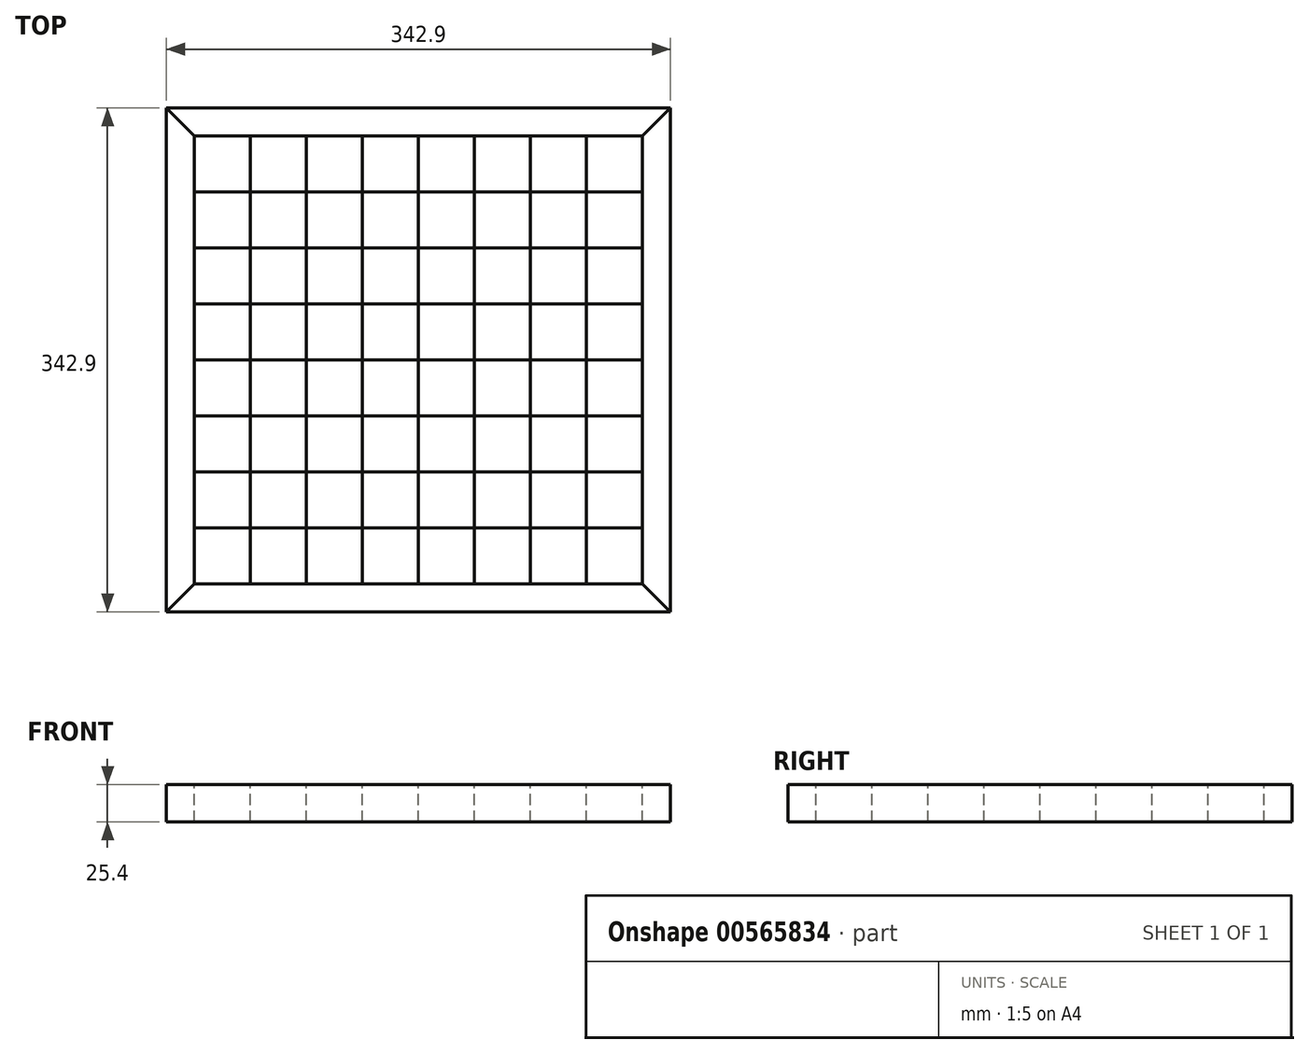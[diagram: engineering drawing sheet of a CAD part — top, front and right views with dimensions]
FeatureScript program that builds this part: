
annotation { "Feature Type Name" : "Feature", "Feature Type Description" : "" }
export const myFeature = defineFeature(function(context is Context, id is Id, definition is map)
    precondition{}
    {
        {
            var Q0;
            Q0=qCreatedBy(makeId("Top.planeOp"),FACE);
            var sketch = newSketch(context, id + "F0", { "sketchPlane" : qUnion([Q0])});
            skLineSegment(sketch, "E0.bottom", {"start": v(-171.45, 171.45) * mm, "end": v(171.45, 171.45) * mm});
            skLineSegment(sketch, "E0.top", {"start": v(-171.45, -171.45) * mm, "end": v(171.45, -171.45) * mm});
            skLineSegment(sketch, "E0.left", {"start": v(-171.45, 171.45) * mm, "end": v(-171.45, -171.45) * mm});
            skLineSegment(sketch, "E0.right", {"start": v(171.45, 171.45) * mm, "end": v(171.45, -171.45) * mm});
            skPoint(sketch, "E0.middle", {"position": v(0, 0) * mm});
            skSolve(sketch);
        }
        {
            var Q0;
            Q0=makeQuery(id+"F0.imprint","IMPRINT",FACE,{"disambiguationData":[TD([[makeQuery(id+"F0.imprint","IMPRINT",EDGE,{"derivedFrom":sQuery(id+"F0.wireOp",EDGE,"E0.bottom")}),-1.0]])]});
            var sketch = newSketch(context, id + "F1", { "sketchPlane" : qUnion([Q0])});
            skLineSegment(sketch, "E1.bottom", {"start": v(-152.4, 152.4) * mm, "end": v(152.4, 152.4) * mm});
            skLineSegment(sketch, "E1.top", {"start": v(-152.4, -152.4) * mm, "end": v(152.4, -152.4) * mm});
            skLineSegment(sketch, "E1.left", {"start": v(-152.4, 152.4) * mm, "end": v(-152.4, -152.4) * mm});
            skLineSegment(sketch, "E1.right", {"start": v(152.4, 152.4) * mm, "end": v(152.4, -152.4) * mm});
            skPoint(sketch, "E1.middle", {"position": v(0, 0) * mm});
            skLineSegment(sketch, "E2", {"start": v(-114.3, -152.4) * mm, "end": v(-114.3, 152.4) * mm});
            skLineSegment(sketch, "E3", {"start": v(-152.4, -114.3) * mm, "end": v(152.4, -114.3) * mm});
            skLineSegment(sketch, "E4", {"start": v(-152.4, -76.2) * mm, "end": v(152.4, -76.2) * mm});
            skLineSegment(sketch, "E5", {"start": v(-152.4, -38.1) * mm, "end": v(152.4, -38.1) * mm});
            skLineSegment(sketch, "E6", {"start": v(-152.4, 0) * mm, "end": v(152.4, 0) * mm});
            skLineSegment(sketch, "E7", {"start": v(-152.4, 38.1) * mm, "end": v(152.4, 38.1) * mm});
            skLineSegment(sketch, "E8", {"start": v(-152.4, 76.2) * mm, "end": v(152.4, 76.2) * mm});
            skLineSegment(sketch, "E9", {"start": v(-152.4, 114.3) * mm, "end": v(152.4, 114.3) * mm});
            skLineSegment(sketch, "E10", {"start": v(-76.2, -152.4) * mm, "end": v(-76.2, 152.4) * mm});
            skLineSegment(sketch, "E11", {"start": v(-38.1, -152.4) * mm, "end": v(-38.1, 152.4) * mm});
            skLineSegment(sketch, "E12", {"start": v(0, -152.4) * mm, "end": v(0, 152.4) * mm});
            skLineSegment(sketch, "E13", {"start": v(38.1, -152.4) * mm, "end": v(38.1, 152.4) * mm});
            skLineSegment(sketch, "E14", {"start": v(76.2, -152.4) * mm, "end": v(76.2, 152.4) * mm});
            skLineSegment(sketch, "E15", {"start": v(114.3, -152.4) * mm, "end": v(114.3, 152.4) * mm});
            skSolve(sketch);
        }
        {
            var Q0;
            Q0=makeQuery(id+"F0.imprint","IMPRINT",FACE,{"disambiguationData":[TD([[makeQuery(id+"F0.imprint","IMPRINT",EDGE,{"derivedFrom":sQuery(id+"F0.wireOp",EDGE,"E0.bottom")}),-1.0]])]});
            var sketch = newSketch(context, id + "F2", { "sketchPlane" : qUnion([Q0])});
            skPoint(sketch, "E16.0", {"position": v(-171.45, -171.45) * mm});
            skPoint(sketch, "E17.0", {"position": v(-152.4, -152.4) * mm});
            skPoint(sketch, "E18.0", {"position": v(152.4, -152.4) * mm});
            skPoint(sketch, "E19.0", {"position": v(171.45, -171.45) * mm});
            skPoint(sketch, "E20.0", {"position": v(152.4, 152.4) * mm});
            skPoint(sketch, "E21.0", {"position": v(171.45, 171.45) * mm});
            skPoint(sketch, "E22.0", {"position": v(-152.4, 152.4) * mm});
            skPoint(sketch, "E23.0", {"position": v(-171.45, 171.45) * mm});
            skLineSegment(sketch, "E24.0", {"start": v(-152.4, 152.4) * mm, "end": v(-152.4, -152.4) * mm});
            skLineSegment(sketch, "E25.0", {"start": v(-171.45, 171.45) * mm, "end": v(-171.45, -171.45) * mm});
            skLineSegment(sketch, "E26", {"start": v(-152.4, 152.4) * mm, "end": v(-171.45, 171.45) * mm});
            skLineSegment(sketch, "E27", {"start": v(-171.45, -171.45) * mm, "end": v(-152.4, -152.4) * mm});
            skLineSegment(sketch, "E28.0", {"start": v(-152.4, -152.4) * mm, "end": v(152.4, -152.4) * mm});
            skLineSegment(sketch, "E29.0", {"start": v(-171.45, -171.45) * mm, "end": v(171.45, -171.45) * mm});
            skLineSegment(sketch, "E30", {"start": v(171.45, -171.45) * mm, "end": v(152.4, -152.4) * mm});
            skLineSegment(sketch, "E31.0", {"start": v(171.45, 171.45) * mm, "end": v(171.45, -171.45) * mm});
            skLineSegment(sketch, "E32.0", {"start": v(152.4, 152.4) * mm, "end": v(152.4, -152.4) * mm});
            skLineSegment(sketch, "E33.0", {"start": v(-152.4, 152.4) * mm, "end": v(152.4, 152.4) * mm});
            skLineSegment(sketch, "E34.0", {"start": v(-171.45, 171.45) * mm, "end": v(171.45, 171.45) * mm});
            skLineSegment(sketch, "E35", {"start": v(152.4, 152.4) * mm, "end": v(171.45, 171.45) * mm});
            skSolve(sketch);
        }
        {
            var Q0;
            {var subQ0=sQuery(id+"F1.wireOp",EDGE,"E1.left");var subQ1=sQuery(id+"F1.wireOp",EDGE,"E1.top");var subQ2=makeQuery(id+"F1.imprint","INTERSECT",VERTEX,{"derivedFrom":[subQ1,subQ0]});Q0=makeQuery(id+"F1.imprint","IMPRINT",FACE,{"disambiguationData":[TD([[makeQuery(id+"F1.imprint","IMPRINT",EDGE,{"disambiguationData":[TD([[subQ2,-1.0]])],"derivedFrom":subQ1}),1.0]])]});}
            extrude(context, id + "F3", {"entities" : qUnion([Q0]), "oppositeDirection" : true, "depth" : 25.4 * mm, "offsetDistance" : 25.4 * mm});
        }
        {
            var Q0;
            {var subQ0=sQuery(id+"F1.wireOp",EDGE,"E3");var subQ1=sQuery(id+"F1.wireOp",EDGE,"E1.left");var subQ2=makeQuery(id+"F1.imprint","INTERSECT",VERTEX,{"derivedFrom":[subQ1,subQ0]});Q0=makeQuery(id+"F1.imprint","IMPRINT",FACE,{"disambiguationData":[TD([[makeQuery(id+"F1.imprint","IMPRINT",EDGE,{"disambiguationData":[TD([[subQ2,1.0]])],"derivedFrom":subQ1}),1.0]])]});}
            extrude(context, id + "F4", {"entities" : qUnion([Q0]), "oppositeDirection" : true, "depth" : 25.4 * mm, "offsetDistance" : 25.4 * mm});
        }
        {
            var Q0;
            {var subQ0=sQuery(id+"F1.wireOp",EDGE,"E6");var subQ1=sQuery(id+"F1.wireOp",EDGE,"E1.left");var subQ2=makeQuery(id+"F1.imprint","INTERSECT",VERTEX,{"derivedFrom":[subQ1,subQ0]});Q0=makeQuery(id+"F1.imprint","IMPRINT",FACE,{"disambiguationData":[TD([[makeQuery(id+"F1.imprint","IMPRINT",EDGE,{"disambiguationData":[TD([[subQ2,1.0]])],"derivedFrom":subQ1}),1.0]])]});}
            extrude(context, id + "F5", {"entities" : qUnion([Q0]), "oppositeDirection" : true, "depth" : 25.4 * mm, "offsetDistance" : 25.4 * mm});
        }
        {
            var Q0;
            {var subQ0=sQuery(id+"F1.wireOp",EDGE,"E4");var subQ1=sQuery(id+"F1.wireOp",EDGE,"E1.left");var subQ2=makeQuery(id+"F1.imprint","INTERSECT",VERTEX,{"derivedFrom":[subQ1,subQ0]});Q0=makeQuery(id+"F1.imprint","IMPRINT",FACE,{"disambiguationData":[TD([[makeQuery(id+"F1.imprint","IMPRINT",EDGE,{"disambiguationData":[TD([[subQ2,1.0]])],"derivedFrom":subQ1}),1.0]])]});}
            extrude(context, id + "F6", {"entities" : qUnion([Q0]), "oppositeDirection" : true, "depth" : 25.4 * mm, "offsetDistance" : 25.4 * mm});
        }
        {
            var Q0;
            {var subQ0=sQuery(id+"F1.wireOp",EDGE,"E5");var subQ1=sQuery(id+"F1.wireOp",EDGE,"E1.left");var subQ2=makeQuery(id+"F1.imprint","INTERSECT",VERTEX,{"derivedFrom":[subQ1,subQ0]});Q0=makeQuery(id+"F1.imprint","IMPRINT",FACE,{"disambiguationData":[TD([[makeQuery(id+"F1.imprint","IMPRINT",EDGE,{"disambiguationData":[TD([[subQ2,1.0]])],"derivedFrom":subQ1}),1.0]])]});}
            extrude(context, id + "F7", {"entities" : qUnion([Q0]), "oppositeDirection" : true, "depth" : 25.4 * mm, "offsetDistance" : 25.4 * mm});
        }
        {
            var Q0;
            {var subQ0=sQuery(id+"F1.wireOp",EDGE,"E7");var subQ1=sQuery(id+"F1.wireOp",EDGE,"E1.left");var subQ2=makeQuery(id+"F1.imprint","INTERSECT",VERTEX,{"derivedFrom":[subQ1,subQ0]});Q0=makeQuery(id+"F1.imprint","IMPRINT",FACE,{"disambiguationData":[TD([[makeQuery(id+"F1.imprint","IMPRINT",EDGE,{"disambiguationData":[TD([[subQ2,1.0]])],"derivedFrom":subQ1}),1.0]])]});}
            extrude(context, id + "F8", {"entities" : qUnion([Q0]), "oppositeDirection" : true, "depth" : 25.4 * mm, "offsetDistance" : 25.4 * mm});
        }
        {
            var Q0;
            {var subQ0=sQuery(id+"F1.wireOp",EDGE,"E8");var subQ1=sQuery(id+"F1.wireOp",EDGE,"E1.left");var subQ2=makeQuery(id+"F1.imprint","INTERSECT",VERTEX,{"derivedFrom":[subQ1,subQ0]});Q0=makeQuery(id+"F1.imprint","IMPRINT",FACE,{"disambiguationData":[TD([[makeQuery(id+"F1.imprint","IMPRINT",EDGE,{"disambiguationData":[TD([[subQ2,1.0]])],"derivedFrom":subQ1}),1.0]])]});}
            extrude(context, id + "F9", {"entities" : qUnion([Q0]), "oppositeDirection" : true, "depth" : 25.4 * mm, "offsetDistance" : 25.4 * mm});
        }
        {
            var Q0;
            {var subQ0=sQuery(id+"F1.wireOp",EDGE,"E1.left");var subQ1=sQuery(id+"F1.wireOp",EDGE,"E1.bottom");var subQ2=makeQuery(id+"F1.imprint","INTERSECT",VERTEX,{"derivedFrom":[subQ1,subQ0]});Q0=makeQuery(id+"F1.imprint","IMPRINT",FACE,{"disambiguationData":[TD([[makeQuery(id+"F1.imprint","IMPRINT",EDGE,{"disambiguationData":[TD([[subQ2,-1.0]])],"derivedFrom":subQ1}),-1.0]])]});}
            extrude(context, id + "F10", {"entities" : qUnion([Q0]), "oppositeDirection" : true, "depth" : 25.4 * mm, "offsetDistance" : 25.4 * mm});
        }
        {
            var Q0;
            {var subQ0=sQuery(id+"F1.wireOp",EDGE,"E2");var subQ1=sQuery(id+"F1.wireOp",EDGE,"E1.bottom");var subQ2=makeQuery(id+"F1.imprint","INTERSECT",VERTEX,{"derivedFrom":[subQ1,subQ0]});Q0=makeQuery(id+"F1.imprint","IMPRINT",FACE,{"disambiguationData":[TD([[makeQuery(id+"F1.imprint","IMPRINT",EDGE,{"disambiguationData":[TD([[subQ2,-1.0]])],"derivedFrom":subQ1}),-1.0]])]});}
            extrude(context, id + "F11", {"entities" : qUnion([Q0]), "oppositeDirection" : true, "depth" : 25.4 * mm, "offsetDistance" : 25.4 * mm});
        }
        {
            var Q0;
            {var subQ0=sQuery(id+"F1.wireOp",EDGE,"E8");var subQ1=sQuery(id+"F1.wireOp",EDGE,"E2");var subQ2=makeQuery(id+"F1.imprint","INTERSECT",VERTEX,{"derivedFrom":[subQ1,subQ0]});Q0=makeQuery(id+"F1.imprint","IMPRINT",FACE,{"disambiguationData":[TD([[makeQuery(id+"F1.imprint","IMPRINT",EDGE,{"disambiguationData":[TD([[subQ2,-1.0]])],"derivedFrom":subQ1}),-1.0]])]});}
            extrude(context, id + "F12", {"entities" : qUnion([Q0]), "oppositeDirection" : true, "depth" : 25.4 * mm, "offsetDistance" : 25.4 * mm});
        }
        {
            var Q0;
            {var subQ0=sQuery(id+"F1.wireOp",EDGE,"E7");var subQ1=sQuery(id+"F1.wireOp",EDGE,"E2");var subQ2=makeQuery(id+"F1.imprint","INTERSECT",VERTEX,{"derivedFrom":[subQ1,subQ0]});Q0=makeQuery(id+"F1.imprint","IMPRINT",FACE,{"disambiguationData":[TD([[makeQuery(id+"F1.imprint","IMPRINT",EDGE,{"disambiguationData":[TD([[subQ2,-1.0]])],"derivedFrom":subQ1}),-1.0]])]});}
            extrude(context, id + "F13", {"entities" : qUnion([Q0]), "oppositeDirection" : true, "depth" : 25.4 * mm, "offsetDistance" : 25.4 * mm});
        }
        {
            var Q0;
            {var subQ0=sQuery(id+"F1.wireOp",EDGE,"E6");var subQ1=sQuery(id+"F1.wireOp",EDGE,"E2");var subQ2=makeQuery(id+"F1.imprint","INTERSECT",VERTEX,{"derivedFrom":[subQ1,subQ0]});Q0=makeQuery(id+"F1.imprint","IMPRINT",FACE,{"disambiguationData":[TD([[makeQuery(id+"F1.imprint","IMPRINT",EDGE,{"disambiguationData":[TD([[subQ2,-1.0]])],"derivedFrom":subQ1}),-1.0]])]});}
            extrude(context, id + "F14", {"entities" : qUnion([Q0]), "oppositeDirection" : true, "depth" : 25.4 * mm, "offsetDistance" : 25.4 * mm});
        }
        {
            var Q0;
            {var subQ0=sQuery(id+"F1.wireOp",EDGE,"E5");var subQ1=sQuery(id+"F1.wireOp",EDGE,"E2");var subQ2=makeQuery(id+"F1.imprint","INTERSECT",VERTEX,{"derivedFrom":[subQ1,subQ0]});Q0=makeQuery(id+"F1.imprint","IMPRINT",FACE,{"disambiguationData":[TD([[makeQuery(id+"F1.imprint","IMPRINT",EDGE,{"disambiguationData":[TD([[subQ2,-1.0]])],"derivedFrom":subQ1}),-1.0]])]});}
            extrude(context, id + "F15", {"entities" : qUnion([Q0]), "oppositeDirection" : true, "depth" : 25.4 * mm, "offsetDistance" : 25.4 * mm});
        }
        {
            var Q0;
            {var subQ0=sQuery(id+"F1.wireOp",EDGE,"E4");var subQ1=sQuery(id+"F1.wireOp",EDGE,"E2");var subQ2=makeQuery(id+"F1.imprint","INTERSECT",VERTEX,{"derivedFrom":[subQ1,subQ0]});Q0=makeQuery(id+"F1.imprint","IMPRINT",FACE,{"disambiguationData":[TD([[makeQuery(id+"F1.imprint","IMPRINT",EDGE,{"disambiguationData":[TD([[subQ2,-1.0]])],"derivedFrom":subQ1}),-1.0]])]});}
            extrude(context, id + "F16", {"entities" : qUnion([Q0]), "oppositeDirection" : true, "depth" : 25.4 * mm, "offsetDistance" : 25.4 * mm});
        }
        {
            var Q0;
            {var subQ0=sQuery(id+"F1.wireOp",EDGE,"E3");var subQ1=sQuery(id+"F1.wireOp",EDGE,"E2");var subQ2=makeQuery(id+"F1.imprint","INTERSECT",VERTEX,{"derivedFrom":[subQ1,subQ0]});Q0=makeQuery(id+"F1.imprint","IMPRINT",FACE,{"disambiguationData":[TD([[makeQuery(id+"F1.imprint","IMPRINT",EDGE,{"disambiguationData":[TD([[subQ2,-1.0]])],"derivedFrom":subQ1}),-1.0]])]});}
            extrude(context, id + "F17", {"entities" : qUnion([Q0]), "oppositeDirection" : true, "depth" : 25.4 * mm, "offsetDistance" : 25.4 * mm});
        }
        {
            var Q0;
            {var subQ0=sQuery(id+"F1.wireOp",EDGE,"E2");var subQ1=sQuery(id+"F1.wireOp",EDGE,"E1.top");var subQ2=makeQuery(id+"F1.imprint","INTERSECT",VERTEX,{"derivedFrom":[subQ1,subQ0]});Q0=makeQuery(id+"F1.imprint","IMPRINT",FACE,{"disambiguationData":[TD([[makeQuery(id+"F1.imprint","IMPRINT",EDGE,{"disambiguationData":[TD([[subQ2,-1.0]])],"derivedFrom":subQ1}),1.0]])]});}
            extrude(context, id + "F18", {"entities" : qUnion([Q0]), "oppositeDirection" : true, "depth" : 25.4 * mm, "offsetDistance" : 25.4 * mm});
        }
        {
            var Q0;
            {var subQ0=sQuery(id+"F1.wireOp",EDGE,"E10");var subQ1=sQuery(id+"F1.wireOp",EDGE,"E1.bottom");var subQ2=makeQuery(id+"F1.imprint","INTERSECT",VERTEX,{"derivedFrom":[subQ1,subQ0]});Q0=makeQuery(id+"F1.imprint","IMPRINT",FACE,{"disambiguationData":[TD([[makeQuery(id+"F1.imprint","IMPRINT",EDGE,{"disambiguationData":[TD([[subQ2,-1.0]])],"derivedFrom":subQ1}),-1.0]])]});}
            extrude(context, id + "F19", {"entities" : qUnion([Q0]), "oppositeDirection" : true, "depth" : 25.4 * mm, "offsetDistance" : 25.4 * mm});
        }
        {
            var Q0;
            {var subQ0=sQuery(id+"F1.wireOp",EDGE,"E10");var subQ1=sQuery(id+"F1.wireOp",EDGE,"E8");var subQ2=makeQuery(id+"F1.imprint","INTERSECT",VERTEX,{"derivedFrom":[subQ1,subQ0]});Q0=makeQuery(id+"F1.imprint","IMPRINT",FACE,{"disambiguationData":[TD([[makeQuery(id+"F1.imprint","IMPRINT",EDGE,{"disambiguationData":[TD([[subQ2,-1.0]])],"derivedFrom":subQ1}),1.0]])]});}
            extrude(context, id + "F20", {"entities" : qUnion([Q0]), "oppositeDirection" : true, "depth" : 25.4 * mm, "offsetDistance" : 25.4 * mm});
        }
        {
            var Q0;
            {var subQ0=sQuery(id+"F1.wireOp",EDGE,"E10");var subQ1=sQuery(id+"F1.wireOp",EDGE,"E7");var subQ2=makeQuery(id+"F1.imprint","INTERSECT",VERTEX,{"derivedFrom":[subQ1,subQ0]});Q0=makeQuery(id+"F1.imprint","IMPRINT",FACE,{"disambiguationData":[TD([[makeQuery(id+"F1.imprint","IMPRINT",EDGE,{"disambiguationData":[TD([[subQ2,-1.0]])],"derivedFrom":subQ1}),1.0]])]});}
            extrude(context, id + "F21", {"entities" : qUnion([Q0]), "oppositeDirection" : true, "depth" : 25.4 * mm, "offsetDistance" : 25.4 * mm});
        }
        {
            var Q0;
            {var subQ0=sQuery(id+"F1.wireOp",EDGE,"E10");var subQ1=sQuery(id+"F1.wireOp",EDGE,"E6");var subQ2=makeQuery(id+"F1.imprint","INTERSECT",VERTEX,{"derivedFrom":[subQ1,subQ0]});Q0=makeQuery(id+"F1.imprint","IMPRINT",FACE,{"disambiguationData":[TD([[makeQuery(id+"F1.imprint","IMPRINT",EDGE,{"disambiguationData":[TD([[subQ2,-1.0]])],"derivedFrom":subQ1}),1.0]])]});}
            extrude(context, id + "F22", {"entities" : qUnion([Q0]), "oppositeDirection" : true, "depth" : 25.4 * mm, "offsetDistance" : 25.4 * mm});
        }
        {
            var Q0;
            {var subQ0=sQuery(id+"F1.wireOp",EDGE,"E10");var subQ1=sQuery(id+"F1.wireOp",EDGE,"E5");var subQ2=makeQuery(id+"F1.imprint","INTERSECT",VERTEX,{"derivedFrom":[subQ1,subQ0]});Q0=makeQuery(id+"F1.imprint","IMPRINT",FACE,{"disambiguationData":[TD([[makeQuery(id+"F1.imprint","IMPRINT",EDGE,{"disambiguationData":[TD([[subQ2,-1.0]])],"derivedFrom":subQ1}),1.0]])]});}
            extrude(context, id + "F23", {"entities" : qUnion([Q0]), "oppositeDirection" : true, "depth" : 25.4 * mm, "offsetDistance" : 25.4 * mm});
        }
        {
            var Q0;
            {var subQ0=sQuery(id+"F1.wireOp",EDGE,"E10");var subQ1=sQuery(id+"F1.wireOp",EDGE,"E4");var subQ2=makeQuery(id+"F1.imprint","INTERSECT",VERTEX,{"derivedFrom":[subQ1,subQ0]});Q0=makeQuery(id+"F1.imprint","IMPRINT",FACE,{"disambiguationData":[TD([[makeQuery(id+"F1.imprint","IMPRINT",EDGE,{"disambiguationData":[TD([[subQ2,-1.0]])],"derivedFrom":subQ1}),1.0]])]});}
            extrude(context, id + "F24", {"entities" : qUnion([Q0]), "oppositeDirection" : true, "depth" : 25.4 * mm, "offsetDistance" : 25.4 * mm});
        }
        {
            var Q0;
            {var subQ0=sQuery(id+"F1.wireOp",EDGE,"E10");var subQ1=sQuery(id+"F1.wireOp",EDGE,"E3");var subQ2=makeQuery(id+"F1.imprint","INTERSECT",VERTEX,{"derivedFrom":[subQ1,subQ0]});Q0=makeQuery(id+"F1.imprint","IMPRINT",FACE,{"disambiguationData":[TD([[makeQuery(id+"F1.imprint","IMPRINT",EDGE,{"disambiguationData":[TD([[subQ2,-1.0]])],"derivedFrom":subQ1}),1.0]])]});}
            extrude(context, id + "F25", {"entities" : qUnion([Q0]), "oppositeDirection" : true, "depth" : 25.4 * mm, "offsetDistance" : 25.4 * mm});
        }
        {
            var Q0;
            {var subQ0=sQuery(id+"F1.wireOp",EDGE,"E10");var subQ1=sQuery(id+"F1.wireOp",EDGE,"E1.top");var subQ2=makeQuery(id+"F1.imprint","INTERSECT",VERTEX,{"derivedFrom":[subQ1,subQ0]});Q0=makeQuery(id+"F1.imprint","IMPRINT",FACE,{"disambiguationData":[TD([[makeQuery(id+"F1.imprint","IMPRINT",EDGE,{"disambiguationData":[TD([[subQ2,-1.0]])],"derivedFrom":subQ1}),1.0]])]});}
            extrude(context, id + "F26", {"entities" : qUnion([Q0]), "oppositeDirection" : true, "depth" : 25.4 * mm, "offsetDistance" : 25.4 * mm});
        }
        {
            var Q0;
            {var subQ0=sQuery(id+"F1.wireOp",EDGE,"E11");var subQ1=sQuery(id+"F1.wireOp",EDGE,"E1.bottom");var subQ2=makeQuery(id+"F1.imprint","INTERSECT",VERTEX,{"derivedFrom":[subQ1,subQ0]});Q0=makeQuery(id+"F1.imprint","IMPRINT",FACE,{"disambiguationData":[TD([[makeQuery(id+"F1.imprint","IMPRINT",EDGE,{"disambiguationData":[TD([[subQ2,-1.0]])],"derivedFrom":subQ1}),-1.0]])]});}
            extrude(context, id + "F27", {"entities" : qUnion([Q0]), "oppositeDirection" : true, "depth" : 25.4 * mm, "offsetDistance" : 25.4 * mm});
        }
        {
            var Q0;
            {var subQ0=sQuery(id+"F1.wireOp",EDGE,"E11");var subQ1=sQuery(id+"F1.wireOp",EDGE,"E8");var subQ2=makeQuery(id+"F1.imprint","INTERSECT",VERTEX,{"derivedFrom":[subQ1,subQ0]});Q0=makeQuery(id+"F1.imprint","IMPRINT",FACE,{"disambiguationData":[TD([[makeQuery(id+"F1.imprint","IMPRINT",EDGE,{"disambiguationData":[TD([[subQ2,-1.0]])],"derivedFrom":subQ1}),1.0]])]});}
            extrude(context, id + "F28", {"entities" : qUnion([Q0]), "oppositeDirection" : true, "depth" : 25.4 * mm, "offsetDistance" : 25.4 * mm});
        }
        {
            var Q0;
            {var subQ0=sQuery(id+"F1.wireOp",EDGE,"E11");var subQ1=sQuery(id+"F1.wireOp",EDGE,"E7");var subQ2=makeQuery(id+"F1.imprint","INTERSECT",VERTEX,{"derivedFrom":[subQ1,subQ0]});Q0=makeQuery(id+"F1.imprint","IMPRINT",FACE,{"disambiguationData":[TD([[makeQuery(id+"F1.imprint","IMPRINT",EDGE,{"disambiguationData":[TD([[subQ2,-1.0]])],"derivedFrom":subQ1}),1.0]])]});}
            extrude(context, id + "F29", {"entities" : qUnion([Q0]), "oppositeDirection" : true, "depth" : 25.4 * mm, "offsetDistance" : 25.4 * mm});
        }
        {
            var Q0;
            {var subQ0=sQuery(id+"F1.wireOp",EDGE,"E11");var subQ1=sQuery(id+"F1.wireOp",EDGE,"E6");var subQ2=makeQuery(id+"F1.imprint","INTERSECT",VERTEX,{"derivedFrom":[subQ1,subQ0]});Q0=makeQuery(id+"F1.imprint","IMPRINT",FACE,{"disambiguationData":[TD([[makeQuery(id+"F1.imprint","IMPRINT",EDGE,{"disambiguationData":[TD([[subQ2,-1.0]])],"derivedFrom":subQ1}),1.0]])]});}
            extrude(context, id + "F30", {"entities" : qUnion([Q0]), "oppositeDirection" : true, "depth" : 25.4 * mm, "offsetDistance" : 25.4 * mm});
        }
        {
            var Q0;
            {var subQ0=sQuery(id+"F1.wireOp",EDGE,"E11");var subQ1=sQuery(id+"F1.wireOp",EDGE,"E5");var subQ2=makeQuery(id+"F1.imprint","INTERSECT",VERTEX,{"derivedFrom":[subQ1,subQ0]});Q0=makeQuery(id+"F1.imprint","IMPRINT",FACE,{"disambiguationData":[TD([[makeQuery(id+"F1.imprint","IMPRINT",EDGE,{"disambiguationData":[TD([[subQ2,-1.0]])],"derivedFrom":subQ1}),1.0]])]});}
            extrude(context, id + "F31", {"entities" : qUnion([Q0]), "oppositeDirection" : true, "depth" : 25.4 * mm, "offsetDistance" : 25.4 * mm});
        }
        {
            var Q0;
            {var subQ0=sQuery(id+"F1.wireOp",EDGE,"E11");var subQ1=sQuery(id+"F1.wireOp",EDGE,"E4");var subQ2=makeQuery(id+"F1.imprint","INTERSECT",VERTEX,{"derivedFrom":[subQ1,subQ0]});Q0=makeQuery(id+"F1.imprint","IMPRINT",FACE,{"disambiguationData":[TD([[makeQuery(id+"F1.imprint","IMPRINT",EDGE,{"disambiguationData":[TD([[subQ2,-1.0]])],"derivedFrom":subQ1}),1.0]])]});}
            extrude(context, id + "F32", {"entities" : qUnion([Q0]), "oppositeDirection" : true, "depth" : 25.4 * mm, "offsetDistance" : 25.4 * mm});
        }
        {
            var Q0;
            {var subQ0=sQuery(id+"F1.wireOp",EDGE,"E11");var subQ1=sQuery(id+"F1.wireOp",EDGE,"E3");var subQ2=makeQuery(id+"F1.imprint","INTERSECT",VERTEX,{"derivedFrom":[subQ1,subQ0]});Q0=makeQuery(id+"F1.imprint","IMPRINT",FACE,{"disambiguationData":[TD([[makeQuery(id+"F1.imprint","IMPRINT",EDGE,{"disambiguationData":[TD([[subQ2,-1.0]])],"derivedFrom":subQ1}),1.0]])]});}
            extrude(context, id + "F33", {"entities" : qUnion([Q0]), "oppositeDirection" : true, "depth" : 25.4 * mm, "offsetDistance" : 25.4 * mm});
        }
        {
            var Q0;
            {var subQ0=sQuery(id+"F1.wireOp",EDGE,"E11");var subQ1=sQuery(id+"F1.wireOp",EDGE,"E1.top");var subQ2=makeQuery(id+"F1.imprint","INTERSECT",VERTEX,{"derivedFrom":[subQ1,subQ0]});Q0=makeQuery(id+"F1.imprint","IMPRINT",FACE,{"disambiguationData":[TD([[makeQuery(id+"F1.imprint","IMPRINT",EDGE,{"disambiguationData":[TD([[subQ2,-1.0]])],"derivedFrom":subQ1}),1.0]])]});}
            extrude(context, id + "F34", {"entities" : qUnion([Q0]), "oppositeDirection" : true, "depth" : 25.4 * mm, "offsetDistance" : 25.4 * mm});
        }
        {
            var Q0;
            {var subQ0=sQuery(id+"F1.wireOp",EDGE,"E12");var subQ1=sQuery(id+"F1.wireOp",EDGE,"E1.bottom");var subQ2=makeQuery(id+"F1.imprint","INTERSECT",VERTEX,{"derivedFrom":[subQ1,subQ0]});Q0=makeQuery(id+"F1.imprint","IMPRINT",FACE,{"disambiguationData":[TD([[makeQuery(id+"F1.imprint","IMPRINT",EDGE,{"disambiguationData":[TD([[subQ2,-1.0]])],"derivedFrom":subQ1}),-1.0]])]});}
            extrude(context, id + "F35", {"entities" : qUnion([Q0]), "oppositeDirection" : true, "depth" : 25.4 * mm, "offsetDistance" : 25.4 * mm});
        }
        {
            var Q0;
            {var subQ0=sQuery(id+"F1.wireOp",EDGE,"E12");var subQ1=sQuery(id+"F1.wireOp",EDGE,"E8");var subQ2=makeQuery(id+"F1.imprint","INTERSECT",VERTEX,{"derivedFrom":[subQ1,subQ0]});Q0=makeQuery(id+"F1.imprint","IMPRINT",FACE,{"disambiguationData":[TD([[makeQuery(id+"F1.imprint","IMPRINT",EDGE,{"disambiguationData":[TD([[subQ2,-1.0]])],"derivedFrom":subQ1}),1.0]])]});}
            extrude(context, id + "F36", {"entities" : qUnion([Q0]), "oppositeDirection" : true, "depth" : 25.4 * mm, "offsetDistance" : 25.4 * mm});
        }
        {
            var Q0;
            {var subQ0=sQuery(id+"F1.wireOp",EDGE,"E12");var subQ1=sQuery(id+"F1.wireOp",EDGE,"E7");var subQ2=makeQuery(id+"F1.imprint","INTERSECT",VERTEX,{"derivedFrom":[subQ1,subQ0]});Q0=makeQuery(id+"F1.imprint","IMPRINT",FACE,{"disambiguationData":[TD([[makeQuery(id+"F1.imprint","IMPRINT",EDGE,{"disambiguationData":[TD([[subQ2,-1.0]])],"derivedFrom":subQ1}),1.0]])]});}
            extrude(context, id + "F37", {"entities" : qUnion([Q0]), "oppositeDirection" : true, "depth" : 25.4 * mm, "offsetDistance" : 25.4 * mm});
        }
        {
            var Q0;
            {var subQ0=sQuery(id+"F1.wireOp",EDGE,"E12");var subQ1=sQuery(id+"F1.wireOp",EDGE,"E6");var subQ2=makeQuery(id+"F1.imprint","INTERSECT",VERTEX,{"derivedFrom":[subQ1,subQ0]});Q0=makeQuery(id+"F1.imprint","IMPRINT",FACE,{"disambiguationData":[TD([[makeQuery(id+"F1.imprint","IMPRINT",EDGE,{"disambiguationData":[TD([[subQ2,-1.0]])],"derivedFrom":subQ1}),1.0]])]});}
            extrude(context, id + "F38", {"entities" : qUnion([Q0]), "oppositeDirection" : true, "depth" : 25.4 * mm, "offsetDistance" : 25.4 * mm});
        }
        {
            var Q0;
            {var subQ0=sQuery(id+"F1.wireOp",EDGE,"E12");var subQ1=sQuery(id+"F1.wireOp",EDGE,"E5");var subQ2=makeQuery(id+"F1.imprint","INTERSECT",VERTEX,{"derivedFrom":[subQ1,subQ0]});Q0=makeQuery(id+"F1.imprint","IMPRINT",FACE,{"disambiguationData":[TD([[makeQuery(id+"F1.imprint","IMPRINT",EDGE,{"disambiguationData":[TD([[subQ2,-1.0]])],"derivedFrom":subQ1}),1.0]])]});}
            extrude(context, id + "F39", {"entities" : qUnion([Q0]), "oppositeDirection" : true, "depth" : 25.4 * mm, "offsetDistance" : 25.4 * mm});
        }
        {
            var Q0;
            {var subQ0=sQuery(id+"F1.wireOp",EDGE,"E12");var subQ1=sQuery(id+"F1.wireOp",EDGE,"E4");var subQ2=makeQuery(id+"F1.imprint","INTERSECT",VERTEX,{"derivedFrom":[subQ1,subQ0]});Q0=makeQuery(id+"F1.imprint","IMPRINT",FACE,{"disambiguationData":[TD([[makeQuery(id+"F1.imprint","IMPRINT",EDGE,{"disambiguationData":[TD([[subQ2,-1.0]])],"derivedFrom":subQ1}),1.0]])]});}
            extrude(context, id + "F40", {"entities" : qUnion([Q0]), "oppositeDirection" : true, "depth" : 25.4 * mm, "offsetDistance" : 25.4 * mm});
        }
        {
            var Q0;
            {var subQ0=sQuery(id+"F1.wireOp",EDGE,"E12");var subQ1=sQuery(id+"F1.wireOp",EDGE,"E3");var subQ2=makeQuery(id+"F1.imprint","INTERSECT",VERTEX,{"derivedFrom":[subQ1,subQ0]});Q0=makeQuery(id+"F1.imprint","IMPRINT",FACE,{"disambiguationData":[TD([[makeQuery(id+"F1.imprint","IMPRINT",EDGE,{"disambiguationData":[TD([[subQ2,-1.0]])],"derivedFrom":subQ1}),1.0]])]});}
            extrude(context, id + "F41", {"entities" : qUnion([Q0]), "oppositeDirection" : true, "depth" : 25.4 * mm, "offsetDistance" : 25.4 * mm});
        }
        {
            var Q0;
            {var subQ0=sQuery(id+"F1.wireOp",EDGE,"E12");var subQ1=sQuery(id+"F1.wireOp",EDGE,"E1.top");var subQ2=makeQuery(id+"F1.imprint","INTERSECT",VERTEX,{"derivedFrom":[subQ1,subQ0]});Q0=makeQuery(id+"F1.imprint","IMPRINT",FACE,{"disambiguationData":[TD([[makeQuery(id+"F1.imprint","IMPRINT",EDGE,{"disambiguationData":[TD([[subQ2,-1.0]])],"derivedFrom":subQ1}),1.0]])]});}
            extrude(context, id + "F42", {"entities" : qUnion([Q0]), "oppositeDirection" : true, "depth" : 25.4 * mm, "offsetDistance" : 25.4 * mm});
        }
        {
            var Q0;
            {var subQ0=sQuery(id+"F1.wireOp",EDGE,"E13");var subQ1=sQuery(id+"F1.wireOp",EDGE,"E1.bottom");var subQ2=makeQuery(id+"F1.imprint","INTERSECT",VERTEX,{"derivedFrom":[subQ1,subQ0]});Q0=makeQuery(id+"F1.imprint","IMPRINT",FACE,{"disambiguationData":[TD([[makeQuery(id+"F1.imprint","IMPRINT",EDGE,{"disambiguationData":[TD([[subQ2,-1.0]])],"derivedFrom":subQ1}),-1.0]])]});}
            extrude(context, id + "F43", {"entities" : qUnion([Q0]), "oppositeDirection" : true, "depth" : 25.4 * mm, "offsetDistance" : 25.4 * mm});
        }
        {
            var Q0;
            {var subQ0=sQuery(id+"F1.wireOp",EDGE,"E13");var subQ1=sQuery(id+"F1.wireOp",EDGE,"E8");var subQ2=makeQuery(id+"F1.imprint","INTERSECT",VERTEX,{"derivedFrom":[subQ1,subQ0]});Q0=makeQuery(id+"F1.imprint","IMPRINT",FACE,{"disambiguationData":[TD([[makeQuery(id+"F1.imprint","IMPRINT",EDGE,{"disambiguationData":[TD([[subQ2,-1.0]])],"derivedFrom":subQ1}),1.0]])]});}
            extrude(context, id + "F44", {"entities" : qUnion([Q0]), "oppositeDirection" : true, "depth" : 25.4 * mm, "offsetDistance" : 25.4 * mm});
        }
        {
            var Q0;
            {var subQ0=sQuery(id+"F1.wireOp",EDGE,"E13");var subQ1=sQuery(id+"F1.wireOp",EDGE,"E7");var subQ2=makeQuery(id+"F1.imprint","INTERSECT",VERTEX,{"derivedFrom":[subQ1,subQ0]});Q0=makeQuery(id+"F1.imprint","IMPRINT",FACE,{"disambiguationData":[TD([[makeQuery(id+"F1.imprint","IMPRINT",EDGE,{"disambiguationData":[TD([[subQ2,-1.0]])],"derivedFrom":subQ1}),1.0]])]});}
            extrude(context, id + "F45", {"entities" : qUnion([Q0]), "oppositeDirection" : true, "depth" : 25.4 * mm, "offsetDistance" : 25.4 * mm});
        }
        {
            var Q0;
            {var subQ0=sQuery(id+"F1.wireOp",EDGE,"E13");var subQ1=sQuery(id+"F1.wireOp",EDGE,"E6");var subQ2=makeQuery(id+"F1.imprint","INTERSECT",VERTEX,{"derivedFrom":[subQ1,subQ0]});Q0=makeQuery(id+"F1.imprint","IMPRINT",FACE,{"disambiguationData":[TD([[makeQuery(id+"F1.imprint","IMPRINT",EDGE,{"disambiguationData":[TD([[subQ2,-1.0]])],"derivedFrom":subQ1}),1.0]])]});}
            extrude(context, id + "F46", {"entities" : qUnion([Q0]), "oppositeDirection" : true, "depth" : 25.4 * mm, "offsetDistance" : 25.4 * mm});
        }
        {
            var Q0;
            {var subQ0=sQuery(id+"F1.wireOp",EDGE,"E13");var subQ1=sQuery(id+"F1.wireOp",EDGE,"E5");var subQ2=makeQuery(id+"F1.imprint","INTERSECT",VERTEX,{"derivedFrom":[subQ1,subQ0]});Q0=makeQuery(id+"F1.imprint","IMPRINT",FACE,{"disambiguationData":[TD([[makeQuery(id+"F1.imprint","IMPRINT",EDGE,{"disambiguationData":[TD([[subQ2,-1.0]])],"derivedFrom":subQ1}),1.0]])]});}
            extrude(context, id + "F47", {"entities" : qUnion([Q0]), "oppositeDirection" : true, "depth" : 25.4 * mm, "offsetDistance" : 25.4 * mm});
        }
        {
            var Q0;
            {var subQ0=sQuery(id+"F1.wireOp",EDGE,"E13");var subQ1=sQuery(id+"F1.wireOp",EDGE,"E4");var subQ2=makeQuery(id+"F1.imprint","INTERSECT",VERTEX,{"derivedFrom":[subQ1,subQ0]});Q0=makeQuery(id+"F1.imprint","IMPRINT",FACE,{"disambiguationData":[TD([[makeQuery(id+"F1.imprint","IMPRINT",EDGE,{"disambiguationData":[TD([[subQ2,-1.0]])],"derivedFrom":subQ1}),1.0]])]});}
            extrude(context, id + "F48", {"entities" : qUnion([Q0]), "oppositeDirection" : true, "depth" : 25.4 * mm, "offsetDistance" : 25.4 * mm});
        }
        {
            var Q0;
            {var subQ0=sQuery(id+"F1.wireOp",EDGE,"E13");var subQ1=sQuery(id+"F1.wireOp",EDGE,"E3");var subQ2=makeQuery(id+"F1.imprint","INTERSECT",VERTEX,{"derivedFrom":[subQ1,subQ0]});Q0=makeQuery(id+"F1.imprint","IMPRINT",FACE,{"disambiguationData":[TD([[makeQuery(id+"F1.imprint","IMPRINT",EDGE,{"disambiguationData":[TD([[subQ2,-1.0]])],"derivedFrom":subQ1}),1.0]])]});}
            extrude(context, id + "F49", {"entities" : qUnion([Q0]), "oppositeDirection" : true, "depth" : 25.4 * mm, "offsetDistance" : 25.4 * mm});
        }
        {
            var Q0;
            {var subQ0=sQuery(id+"F1.wireOp",EDGE,"E13");var subQ1=sQuery(id+"F1.wireOp",EDGE,"E1.top");var subQ2=makeQuery(id+"F1.imprint","INTERSECT",VERTEX,{"derivedFrom":[subQ1,subQ0]});Q0=makeQuery(id+"F1.imprint","IMPRINT",FACE,{"disambiguationData":[TD([[makeQuery(id+"F1.imprint","IMPRINT",EDGE,{"disambiguationData":[TD([[subQ2,-1.0]])],"derivedFrom":subQ1}),1.0]])]});}
            extrude(context, id + "F50", {"entities" : qUnion([Q0]), "oppositeDirection" : true, "depth" : 25.4 * mm, "offsetDistance" : 25.4 * mm});
        }
        {
            var Q0;
            {var subQ0=sQuery(id+"F1.wireOp",EDGE,"E14");var subQ1=sQuery(id+"F1.wireOp",EDGE,"E1.bottom");var subQ2=makeQuery(id+"F1.imprint","INTERSECT",VERTEX,{"derivedFrom":[subQ1,subQ0]});Q0=makeQuery(id+"F1.imprint","IMPRINT",FACE,{"disambiguationData":[TD([[makeQuery(id+"F1.imprint","IMPRINT",EDGE,{"disambiguationData":[TD([[subQ2,-1.0]])],"derivedFrom":subQ1}),-1.0]])]});}
            extrude(context, id + "F51", {"entities" : qUnion([Q0]), "oppositeDirection" : true, "depth" : 25.4 * mm, "offsetDistance" : 25.4 * mm});
        }
        {
            var Q0;
            {var subQ0=sQuery(id+"F1.wireOp",EDGE,"E14");var subQ1=sQuery(id+"F1.wireOp",EDGE,"E8");var subQ2=makeQuery(id+"F1.imprint","INTERSECT",VERTEX,{"derivedFrom":[subQ1,subQ0]});Q0=makeQuery(id+"F1.imprint","IMPRINT",FACE,{"disambiguationData":[TD([[makeQuery(id+"F1.imprint","IMPRINT",EDGE,{"disambiguationData":[TD([[subQ2,-1.0]])],"derivedFrom":subQ1}),1.0]])]});}
            extrude(context, id + "F52", {"entities" : qUnion([Q0]), "oppositeDirection" : true, "depth" : 25.4 * mm, "offsetDistance" : 25.4 * mm});
        }
        {
            var Q0;
            {var subQ0=sQuery(id+"F1.wireOp",EDGE,"E14");var subQ1=sQuery(id+"F1.wireOp",EDGE,"E7");var subQ2=makeQuery(id+"F1.imprint","INTERSECT",VERTEX,{"derivedFrom":[subQ1,subQ0]});Q0=makeQuery(id+"F1.imprint","IMPRINT",FACE,{"disambiguationData":[TD([[makeQuery(id+"F1.imprint","IMPRINT",EDGE,{"disambiguationData":[TD([[subQ2,-1.0]])],"derivedFrom":subQ1}),1.0]])]});}
            extrude(context, id + "F53", {"entities" : qUnion([Q0]), "oppositeDirection" : true, "depth" : 25.4 * mm, "offsetDistance" : 25.4 * mm});
        }
        {
            var Q0;
            {var subQ0=sQuery(id+"F1.wireOp",EDGE,"E14");var subQ1=sQuery(id+"F1.wireOp",EDGE,"E6");var subQ2=makeQuery(id+"F1.imprint","INTERSECT",VERTEX,{"derivedFrom":[subQ1,subQ0]});Q0=makeQuery(id+"F1.imprint","IMPRINT",FACE,{"disambiguationData":[TD([[makeQuery(id+"F1.imprint","IMPRINT",EDGE,{"disambiguationData":[TD([[subQ2,-1.0]])],"derivedFrom":subQ1}),1.0]])]});}
            extrude(context, id + "F54", {"entities" : qUnion([Q0]), "oppositeDirection" : true, "depth" : 25.4 * mm, "offsetDistance" : 25.4 * mm});
        }
        {
            var Q0;
            {var subQ0=sQuery(id+"F1.wireOp",EDGE,"E14");var subQ1=sQuery(id+"F1.wireOp",EDGE,"E5");var subQ2=makeQuery(id+"F1.imprint","INTERSECT",VERTEX,{"derivedFrom":[subQ1,subQ0]});Q0=makeQuery(id+"F1.imprint","IMPRINT",FACE,{"disambiguationData":[TD([[makeQuery(id+"F1.imprint","IMPRINT",EDGE,{"disambiguationData":[TD([[subQ2,-1.0]])],"derivedFrom":subQ1}),1.0]])]});}
            extrude(context, id + "F55", {"entities" : qUnion([Q0]), "oppositeDirection" : true, "depth" : 25.4 * mm, "offsetDistance" : 25.4 * mm});
        }
        {
            var Q0;
            {var subQ0=sQuery(id+"F1.wireOp",EDGE,"E14");var subQ1=sQuery(id+"F1.wireOp",EDGE,"E4");var subQ2=makeQuery(id+"F1.imprint","INTERSECT",VERTEX,{"derivedFrom":[subQ1,subQ0]});Q0=makeQuery(id+"F1.imprint","IMPRINT",FACE,{"disambiguationData":[TD([[makeQuery(id+"F1.imprint","IMPRINT",EDGE,{"disambiguationData":[TD([[subQ2,-1.0]])],"derivedFrom":subQ1}),1.0]])]});}
            extrude(context, id + "F56", {"entities" : qUnion([Q0]), "oppositeDirection" : true, "depth" : 25.4 * mm, "offsetDistance" : 25.4 * mm});
        }
        {
            var Q0;
            {var subQ0=sQuery(id+"F1.wireOp",EDGE,"E14");var subQ1=sQuery(id+"F1.wireOp",EDGE,"E3");var subQ2=makeQuery(id+"F1.imprint","INTERSECT",VERTEX,{"derivedFrom":[subQ1,subQ0]});Q0=makeQuery(id+"F1.imprint","IMPRINT",FACE,{"disambiguationData":[TD([[makeQuery(id+"F1.imprint","IMPRINT",EDGE,{"disambiguationData":[TD([[subQ2,-1.0]])],"derivedFrom":subQ1}),1.0]])]});}
            extrude(context, id + "F57", {"entities" : qUnion([Q0]), "oppositeDirection" : true, "depth" : 25.4 * mm, "offsetDistance" : 25.4 * mm});
        }
        {
            var Q0;
            {var subQ0=sQuery(id+"F1.wireOp",EDGE,"E14");var subQ1=sQuery(id+"F1.wireOp",EDGE,"E1.top");var subQ2=makeQuery(id+"F1.imprint","INTERSECT",VERTEX,{"derivedFrom":[subQ1,subQ0]});Q0=makeQuery(id+"F1.imprint","IMPRINT",FACE,{"disambiguationData":[TD([[makeQuery(id+"F1.imprint","IMPRINT",EDGE,{"disambiguationData":[TD([[subQ2,-1.0]])],"derivedFrom":subQ1}),1.0]])]});}
            extrude(context, id + "F58", {"entities" : qUnion([Q0]), "oppositeDirection" : true, "depth" : 25.4 * mm, "offsetDistance" : 25.4 * mm});
        }
        {
            var Q0;
            {var subQ0=sQuery(id+"F1.wireOp",EDGE,"E1.right");var subQ1=sQuery(id+"F1.wireOp",EDGE,"E1.bottom");var subQ2=makeQuery(id+"F1.imprint","INTERSECT",VERTEX,{"derivedFrom":[subQ1,subQ0]});Q0=makeQuery(id+"F1.imprint","IMPRINT",FACE,{"disambiguationData":[TD([[makeQuery(id+"F1.imprint","IMPRINT",EDGE,{"disambiguationData":[TD([[subQ2,1.0]])],"derivedFrom":subQ1}),-1.0]])]});}
            extrude(context, id + "F59", {"entities" : qUnion([Q0]), "oppositeDirection" : true, "depth" : 25.4 * mm, "offsetDistance" : 25.4 * mm});
        }
        {
            var Q0;
            {var subQ0=sQuery(id+"F1.wireOp",EDGE,"E8");var subQ1=sQuery(id+"F1.wireOp",EDGE,"E1.right");var subQ2=makeQuery(id+"F1.imprint","INTERSECT",VERTEX,{"derivedFrom":[subQ1,subQ0]});Q0=makeQuery(id+"F1.imprint","IMPRINT",FACE,{"disambiguationData":[TD([[makeQuery(id+"F1.imprint","IMPRINT",EDGE,{"disambiguationData":[TD([[subQ2,1.0]])],"derivedFrom":subQ1}),-1.0]])]});}
            extrude(context, id + "F60", {"entities" : qUnion([Q0]), "oppositeDirection" : true, "depth" : 25.4 * mm, "offsetDistance" : 25.4 * mm});
        }
        {
            var Q0;
            {var subQ0=sQuery(id+"F1.wireOp",EDGE,"E7");var subQ1=sQuery(id+"F1.wireOp",EDGE,"E1.right");var subQ2=makeQuery(id+"F1.imprint","INTERSECT",VERTEX,{"derivedFrom":[subQ1,subQ0]});Q0=makeQuery(id+"F1.imprint","IMPRINT",FACE,{"disambiguationData":[TD([[makeQuery(id+"F1.imprint","IMPRINT",EDGE,{"disambiguationData":[TD([[subQ2,1.0]])],"derivedFrom":subQ1}),-1.0]])]});}
            extrude(context, id + "F61", {"entities" : qUnion([Q0]), "oppositeDirection" : true, "depth" : 25.4 * mm, "offsetDistance" : 25.4 * mm});
        }
        {
            var Q0;
            {var subQ0=sQuery(id+"F1.wireOp",EDGE,"E6");var subQ1=sQuery(id+"F1.wireOp",EDGE,"E1.right");var subQ2=makeQuery(id+"F1.imprint","INTERSECT",VERTEX,{"derivedFrom":[subQ1,subQ0]});Q0=makeQuery(id+"F1.imprint","IMPRINT",FACE,{"disambiguationData":[TD([[makeQuery(id+"F1.imprint","IMPRINT",EDGE,{"disambiguationData":[TD([[subQ2,1.0]])],"derivedFrom":subQ1}),-1.0]])]});}
            extrude(context, id + "F62", {"entities" : qUnion([Q0]), "oppositeDirection" : true, "depth" : 25.4 * mm, "offsetDistance" : 25.4 * mm});
        }
        {
            var Q0;
            {var subQ0=sQuery(id+"F1.wireOp",EDGE,"E5");var subQ1=sQuery(id+"F1.wireOp",EDGE,"E1.right");var subQ2=makeQuery(id+"F1.imprint","INTERSECT",VERTEX,{"derivedFrom":[subQ1,subQ0]});Q0=makeQuery(id+"F1.imprint","IMPRINT",FACE,{"disambiguationData":[TD([[makeQuery(id+"F1.imprint","IMPRINT",EDGE,{"disambiguationData":[TD([[subQ2,1.0]])],"derivedFrom":subQ1}),-1.0]])]});}
            extrude(context, id + "F63", {"entities" : qUnion([Q0]), "oppositeDirection" : true, "depth" : 25.4 * mm, "offsetDistance" : 25.4 * mm});
        }
        {
            var Q0;
            {var subQ0=sQuery(id+"F1.wireOp",EDGE,"E4");var subQ1=sQuery(id+"F1.wireOp",EDGE,"E1.right");var subQ2=makeQuery(id+"F1.imprint","INTERSECT",VERTEX,{"derivedFrom":[subQ1,subQ0]});Q0=makeQuery(id+"F1.imprint","IMPRINT",FACE,{"disambiguationData":[TD([[makeQuery(id+"F1.imprint","IMPRINT",EDGE,{"disambiguationData":[TD([[subQ2,1.0]])],"derivedFrom":subQ1}),-1.0]])]});}
            extrude(context, id + "F64", {"entities" : qUnion([Q0]), "oppositeDirection" : true, "depth" : 25.4 * mm, "offsetDistance" : 25.4 * mm});
        }
        {
            var Q0;
            {var subQ0=sQuery(id+"F1.wireOp",EDGE,"E3");var subQ1=sQuery(id+"F1.wireOp",EDGE,"E1.right");var subQ2=makeQuery(id+"F1.imprint","INTERSECT",VERTEX,{"derivedFrom":[subQ1,subQ0]});Q0=makeQuery(id+"F1.imprint","IMPRINT",FACE,{"disambiguationData":[TD([[makeQuery(id+"F1.imprint","IMPRINT",EDGE,{"disambiguationData":[TD([[subQ2,1.0]])],"derivedFrom":subQ1}),-1.0]])]});}
            extrude(context, id + "F65", {"entities" : qUnion([Q0]), "oppositeDirection" : true, "depth" : 25.4 * mm, "offsetDistance" : 25.4 * mm});
        }
        {
            var Q0;
            {var subQ0=sQuery(id+"F1.wireOp",EDGE,"E1.right");var subQ1=sQuery(id+"F1.wireOp",EDGE,"E1.top");var subQ2=makeQuery(id+"F1.imprint","INTERSECT",VERTEX,{"derivedFrom":[subQ1,subQ0]});Q0=makeQuery(id+"F1.imprint","IMPRINT",FACE,{"disambiguationData":[TD([[makeQuery(id+"F1.imprint","IMPRINT",EDGE,{"disambiguationData":[TD([[subQ2,1.0]])],"derivedFrom":subQ1}),1.0]])]});}
            extrude(context, id + "F66", {"entities" : qUnion([Q0]), "oppositeDirection" : true, "depth" : 25.4 * mm, "offsetDistance" : 25.4 * mm});
        }
        {
            var Q0;
            Q0=makeQuery(id+"F2.imprint","IMPRINT",FACE,{"disambiguationData":[TD([[makeQuery(id+"F2.imprint","IMPRINT",EDGE,{"derivedFrom":sQuery(id+"F2.wireOp",EDGE,"E24.0")}),-1.0]])]});
            extrude(context, id + "F67", {"entities" : qUnion([Q0]), "oppositeDirection" : true, "depth" : 25.4 * mm, "offsetDistance" : 25.4 * mm});
        }
        {
            var Q0;
            Q0=makeQuery(id+"F2.imprint","IMPRINT",FACE,{"disambiguationData":[TD([[makeQuery(id+"F2.imprint","IMPRINT",EDGE,{"derivedFrom":sQuery(id+"F2.wireOp",EDGE,"E26")}),-1.0]])]});
            extrude(context, id + "F68", {"entities" : qUnion([Q0]), "oppositeDirection" : true, "depth" : 25.4 * mm, "offsetDistance" : 25.4 * mm});
        }
        {
            var Q0;
            Q0=makeQuery(id+"F2.imprint","IMPRINT",FACE,{"disambiguationData":[TD([[makeQuery(id+"F2.imprint","IMPRINT",EDGE,{"derivedFrom":sQuery(id+"F2.wireOp",EDGE,"E30")}),-1.0]])]});
            extrude(context, id + "F69", {"entities" : qUnion([Q0]), "oppositeDirection" : true, "depth" : 25.4 * mm, "offsetDistance" : 25.4 * mm});
        }
        {
            var Q0;
            Q0=makeQuery(id+"F2.imprint","IMPRINT",FACE,{"disambiguationData":[TD([[makeQuery(id+"F2.imprint","IMPRINT",EDGE,{"derivedFrom":sQuery(id+"F2.wireOp",EDGE,"E27")}),-1.0]])]});
            extrude(context, id + "F70", {"entities" : qUnion([Q0]), "oppositeDirection" : true, "depth" : 25.4 * mm, "offsetDistance" : 25.4 * mm});
        }
    });
